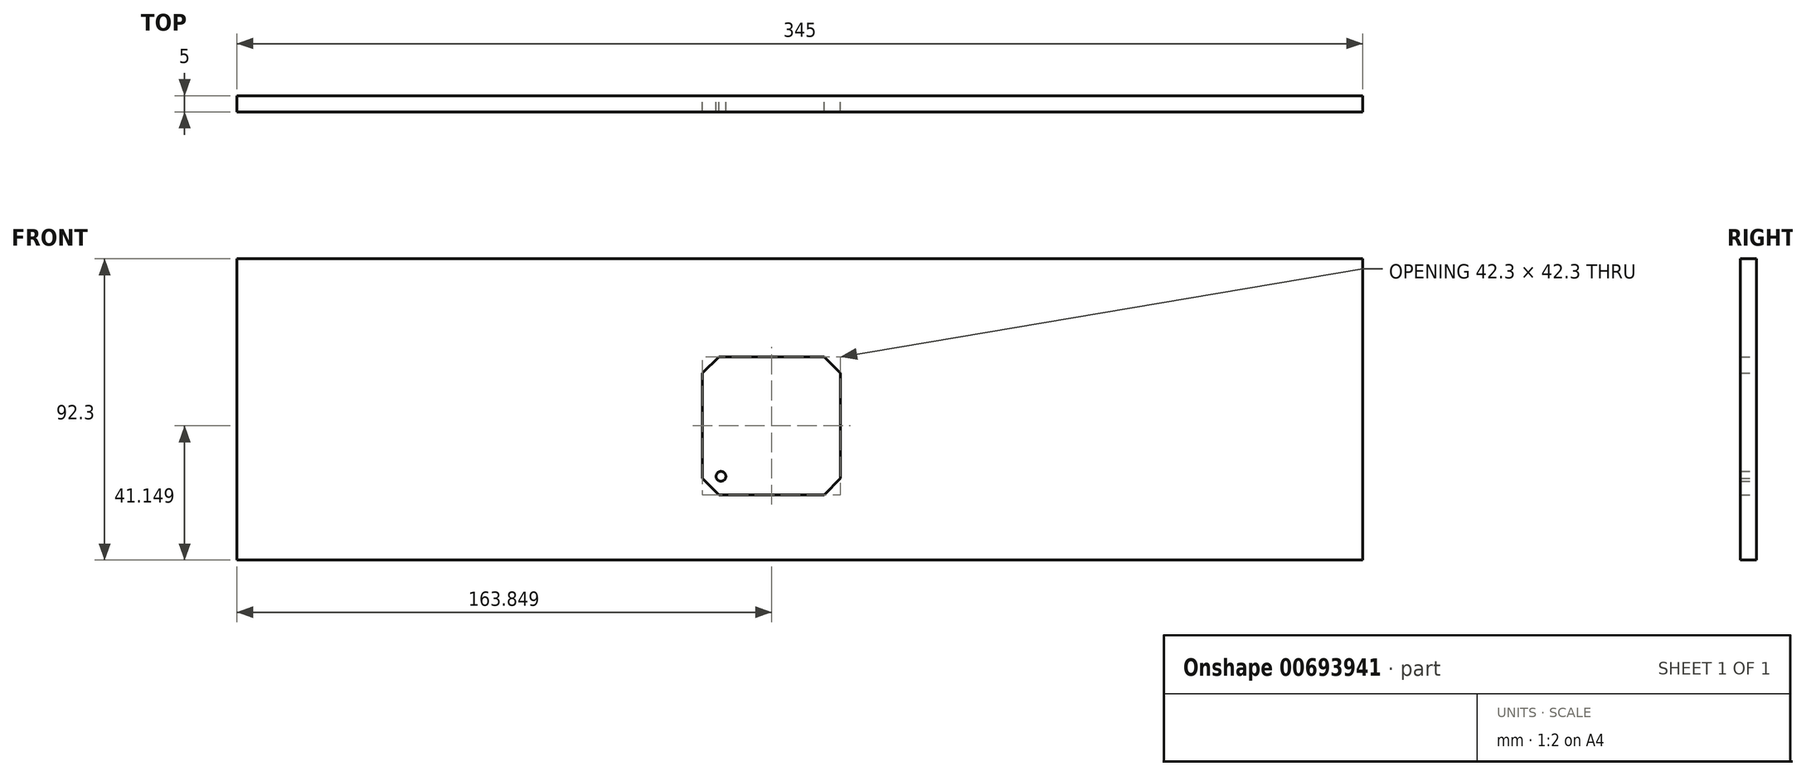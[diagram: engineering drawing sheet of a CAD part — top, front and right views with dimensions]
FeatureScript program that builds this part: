
annotation { "Feature Type Name" : "Feature", "Feature Type Description" : "" }
export const myFeature = defineFeature(function(context is Context, id is Id, definition is map)
    precondition{}
    {
        {
            var Q0;
            Q0=qCreatedBy(makeId("Front.planeOp"),FACE);
            var sketch = newSketch(context, id + "F0", { "sketchPlane" : qUnion([Q0])});
            skCircle(sketch, "E0", {"center": v(-40.1, 7.93) * mm, "radius": 1.5 * mm});
            skCircle(sketch, "E1", {"center": v(-9.1, 7.93) * mm, "radius": 1.5 * mm});
            skCircle(sketch, "E2", {"center": v(-9.1, 38.93) * mm, "radius": 1.5 * mm});
            skCircle(sketch, "E3", {"center": v(-40.1, 38.93) * mm, "radius": 1.5 * mm});
            skLineSegment(sketch, "E4", {"start": v(-45.74, 39.58) * mm, "end": v(-45.74, 7.28) * mm});
            skLineSegment(sketch, "E5", {"start": v(-45.74, 7.28) * mm, "end": v(-40.74, 2.28) * mm});
            skLineSegment(sketch, "E6", {"start": v(-40.74, 2.28) * mm, "end": v(-8.44, 2.28) * mm});
            skLineSegment(sketch, "E7", {"start": v(-8.44, 2.28) * mm, "end": v(-3.44, 7.28) * mm});
            skLineSegment(sketch, "E8", {"start": v(-3.44, 7.28) * mm, "end": v(-3.44, 39.58) * mm});
            skLineSegment(sketch, "E9", {"start": v(-3.44, 39.58) * mm, "end": v(-8.44, 44.58) * mm});
            skLineSegment(sketch, "E10", {"start": v(-8.44, 44.58) * mm, "end": v(-40.74, 44.58) * mm});
            skLineSegment(sketch, "E11", {"start": v(-40.74, 44.58) * mm, "end": v(-45.74, 39.58) * mm});
            skCircle(sketch, "E12", {"center": v(-24.6, 23.43) * mm, "radius": 11.25 * mm});
            skLineSegment(sketch, "E13", {"start": v(-24.6, 23.43) * mm, "end": v(-24.6, 53.9) * mm, "construction": true});
            skLineSegment(sketch, "E14", {"start": v(-40.1, 38.93) * mm, "end": v(-9.1, 7.93) * mm, "construction": true});
            skLineSegment(sketch, "E15.bottom", {"start": v(-188.44, 74.58) * mm, "end": v(156.56, 74.58) * mm});
            skLineSegment(sketch, "E15.top", {"start": v(-188.44, -17.72) * mm, "end": v(156.56, -17.72) * mm});
            skLineSegment(sketch, "E15.left", {"start": v(-188.44, 74.58) * mm, "end": v(-188.44, -17.72) * mm});
            skLineSegment(sketch, "E15.right", {"start": v(156.56, 74.58) * mm, "end": v(156.56, -17.72) * mm});
            skSolve(sketch);
        }
        {
            var Q0;
            Q0 = qSketchRegion(id + "F0", true);
            var Q1;
            Q1=makeQuery(id+"F0.imprint","IMPRINT",FACE,{"disambiguationData":[TD([[makeQuery(id+"F0.imprint","IMPRINT",EDGE,{"derivedFrom":sQuery(id+"F0.wireOp",EDGE,"E0")}),1.0]])]});
            extrude(context, id + "F1", {"entities" : qUnion([Q0, Q1]), "depth" : 5 * mm, "offsetDistance" : 25 * mm});
        }
    });
